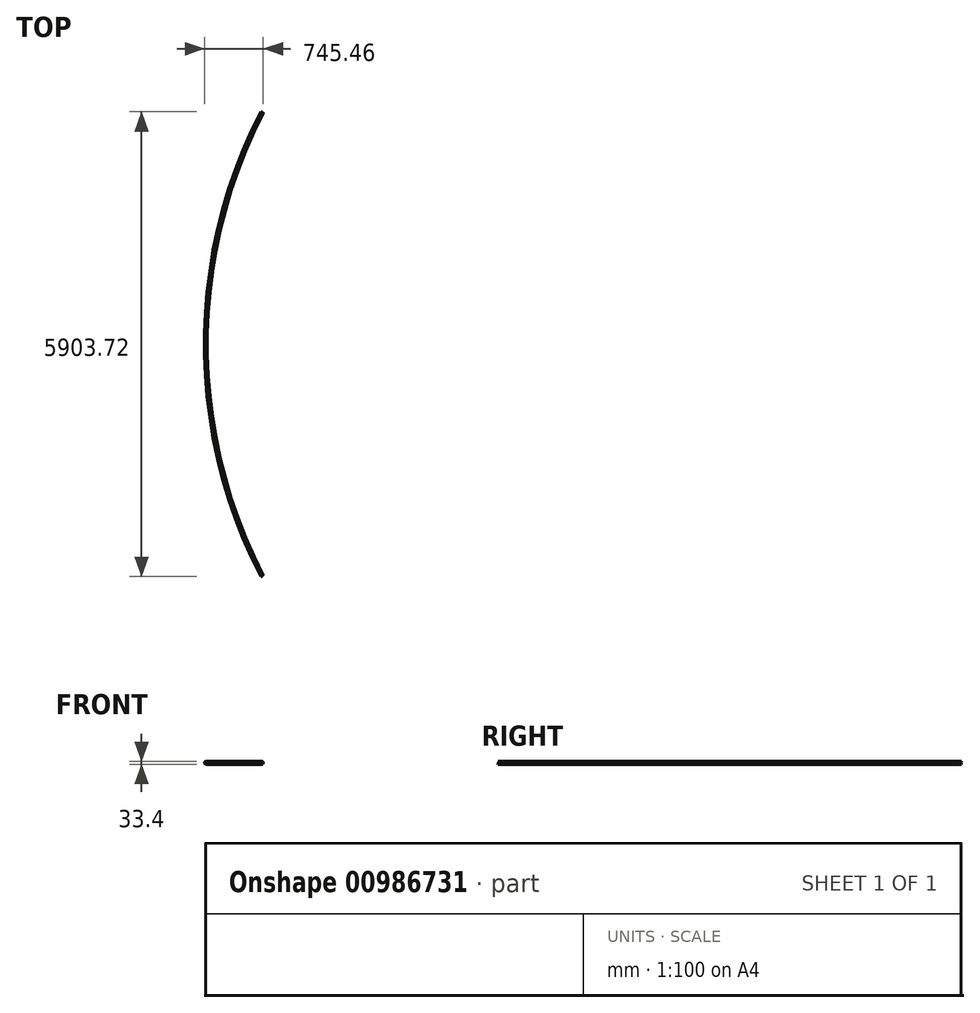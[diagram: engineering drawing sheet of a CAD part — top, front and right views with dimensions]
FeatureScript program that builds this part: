
annotation { "Feature Type Name" : "Feature", "Feature Type Description" : "" }
export const myFeature = defineFeature(function(context is Context, id is Id, definition is map)
    precondition{}
    {
        {
            var Q0;
            Q0=qCreatedBy(makeId("Front.planeOp"),FACE);
            var sketch = newSketch(context, id + "F0", { "sketchPlane" : qUnion([Q0])});
            skCircle(sketch, "E0", {"center": v(0, 0) * mm, "radius": 16.7 * mm});
            skCircle(sketch, "E1.0", {"center": v(0, 0) * mm, "radius": 13.93 * mm});
            skLineSegment(sketch, "E2", {"start": v(0, 0) * mm, "end": v(6428, 0) * mm, "construction": true});
            skLineSegment(sketch, "E3", {"start": v(6428, 0) * mm, "end": v(6428, -200) * mm, "construction": true});
            skSolve(sketch);
        }
        {
            var Q0;
            Q0=qSketchRegion(id+"F0",true);
            var Q1;
            Q1=sQuery(id+"F0.wireOp",EDGE,"E3");
            revolve(context, id + "F1", {"surfaceOperationType" : NewSurfaceOperationType.NEW, "entities" : qUnion([Q0]), "axis" : qUnion([Q1]), "revolveType" : RevolveType.SYMMETRIC, "angle" : 54.52 * degree});
        }
    });
